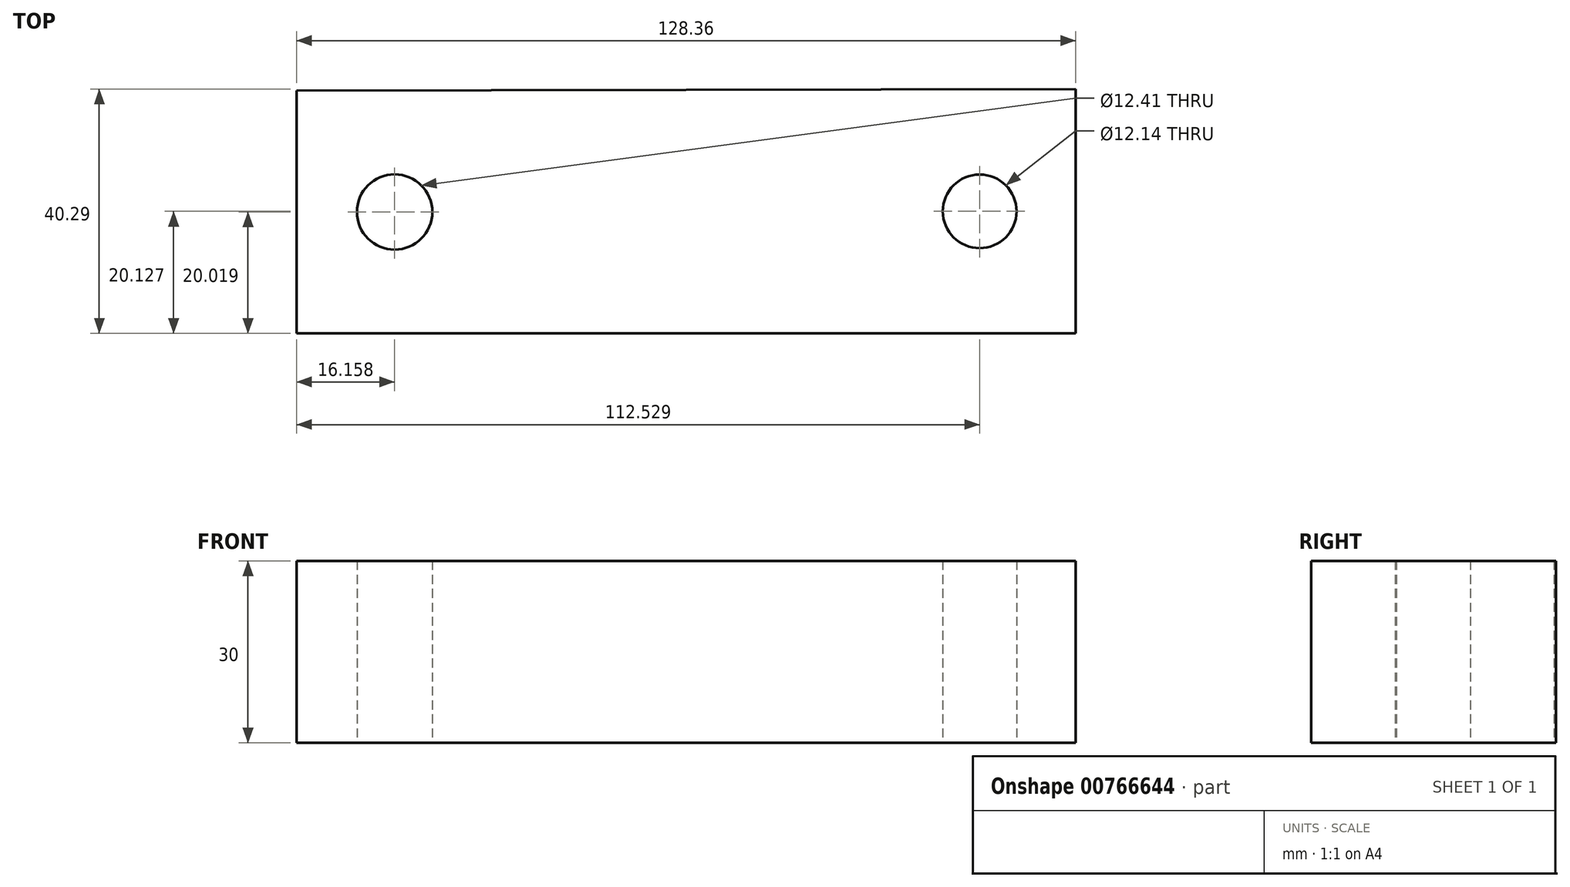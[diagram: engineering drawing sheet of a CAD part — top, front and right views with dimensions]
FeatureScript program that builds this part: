
annotation { "Feature Type Name" : "Feature", "Feature Type Description" : "" }
export const myFeature = defineFeature(function(context is Context, id is Id, definition is map)
    precondition{}
    {
        {
            var Q0;
            Q0=qCreatedBy(makeId("Top.planeOp"),FACE);
            var sketch = newSketch(context, id + "F0", { "sketchPlane" : qUnion([Q0])});
            skLineSegment(sketch, "E0", {"start": v(-51.37, 27.77) * mm, "end": v(-51.37, -12.23) * mm});
            skLineSegment(sketch, "E1", {"start": v(-51.37, -12.23) * mm, "end": v(76.99, -12.23) * mm});
            skLineSegment(sketch, "E2", {"start": v(76.99, -12.23) * mm, "end": v(76.99, 28.06) * mm});
            skLineSegment(sketch, "E3", {"start": v(76.99, 28.06) * mm, "end": v(-51.37, 27.77) * mm});
            skCircle(sketch, "E4", {"center": v(-35.21, 7.79) * mm, "radius": 6.2 * mm});
            skCircle(sketch, "E5", {"center": v(61.16, 7.9) * mm, "radius": 6.07 * mm});
            skSolve(sketch);
        }
        {
            var Q0;
            Q0=makeQuery(id+"F0.imprint","IMPRINT",FACE,{"disambiguationData":[TD([[makeQuery(id+"F0.imprint","IMPRINT",EDGE,{"derivedFrom":sQuery(id+"F0.wireOp",EDGE,"E0")}),1.0]])]});
            extrude(context, id + "F1", {"entities" : qUnion([Q0]), "depth" : 30 * mm, "offsetDistance" : 25 * mm});
        }
    });
